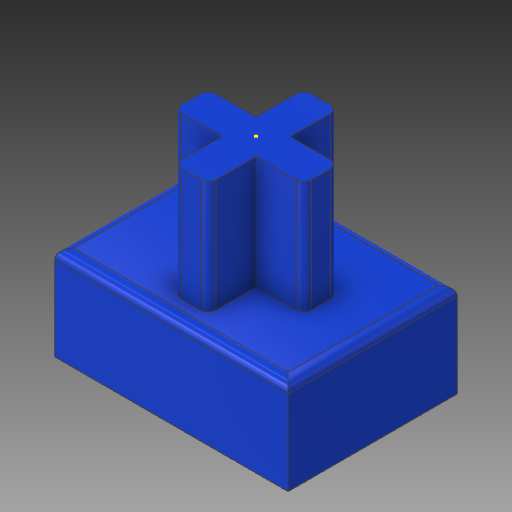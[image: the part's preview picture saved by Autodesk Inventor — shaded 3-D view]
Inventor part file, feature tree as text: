
AUTODESK INVENTOR PART (.ipt)
format: ipt  version: 2018 (Build 220112000, 112)  size: 174,080 bytes
history: native  units: in
note: dims shown in document units (in); Inventor stores cm internally (conversion verified against a paired STEP export)
features: other x3, extrude x2, fillet x2
ambient origin geometry x8: Origin, YZ Plane, XZ Plane, XY Plane, X Axis, Y Axis, Z Axis, Center Point
bodies: Solid1 (feature_tree)
feature tree (7):
  extrude  "Pole Base"  Depth=0.2933in
  extrude  "Pole"  Depth=0.2126in
  fillet  "Pole Rounding"  Radius=0.1181in
  fillet  "Base Rounding"  Radius=0.1417in
  other  "Top Center Point"
  other  "Pole Base Profile"
  other  "Cross Base"
